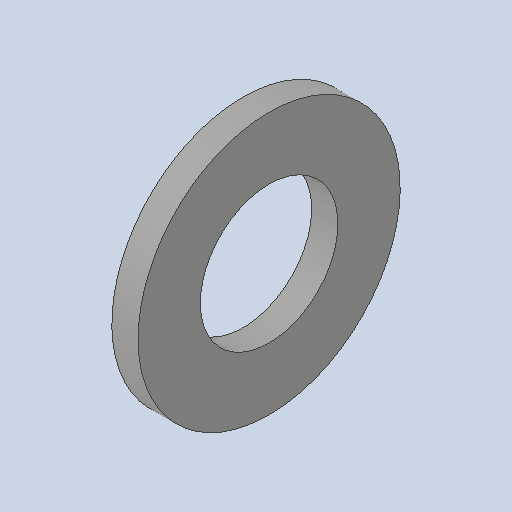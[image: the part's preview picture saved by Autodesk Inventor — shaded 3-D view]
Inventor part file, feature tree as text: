
AUTODESK INVENTOR PART (.ipt)
format: ipt  version: 2023 (Build 270158000, 158)  size: 114,176 bytes
history: native  units: mm
features: other x7, extrude x1, sketch x1
ambient origin geometry x8: Origin, YZ Plane, XZ Plane, XY Plane, X Axis, Y Axis, Z Axis, Center Point
bodies: Solid1 (feature_tree)
feature tree (9):
  extrude  "Extrusion1"  TaperAngle=0.0deg  [1 undecoded]
  other  "BLS_1_XY"
  other  "BLS_1_YZ"
  other  "BLS_1_ZX"
  other  "BLS_1_X"
  other  "BLS_1_Y"
  other  "BLS_1_Z"
  other  "BLS_1_Center"
  sketch  "Skizze_1"  dims[d0=1.6mm d1=0.0mm d2=0.0mm]
note: 1 required parameter value undecoded (feature->parameter linkage not recoverable at this tier; creation-order binding heuristic only, values carry confidence <= 0.55)
